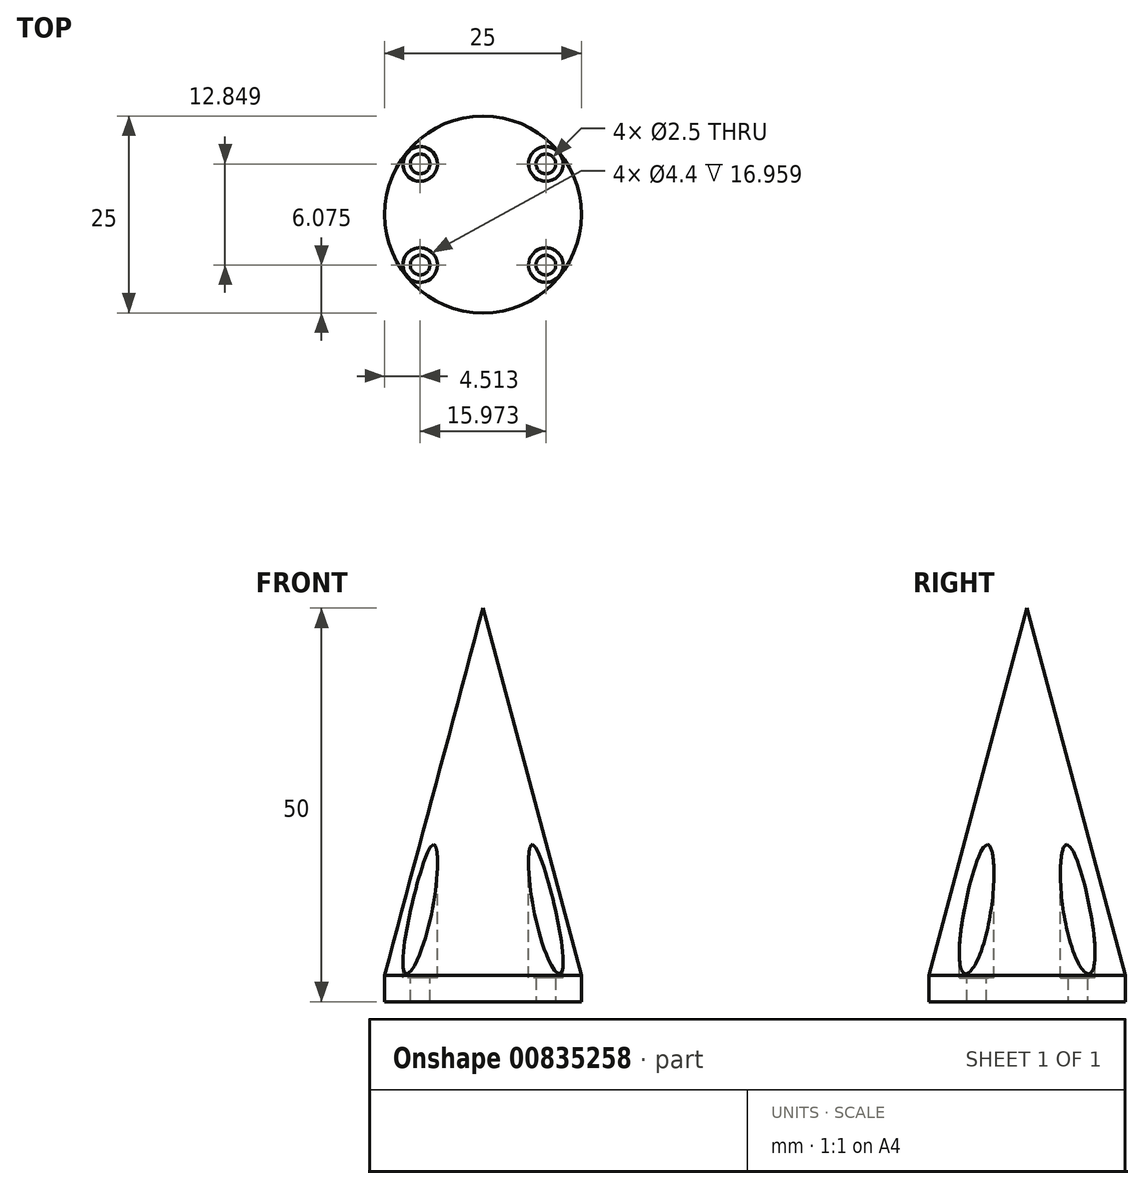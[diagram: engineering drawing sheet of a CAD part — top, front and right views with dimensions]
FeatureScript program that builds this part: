
annotation { "Feature Type Name" : "Feature", "Feature Type Description" : "" }
export const myFeature = defineFeature(function(context is Context, id is Id, definition is map)
    precondition{}
    {
        {
            var Q0;
            Q0=qCreatedBy(makeId("Top.planeOp"),FACE);
            var sketch = newSketch(context, id + "F0", { "sketchPlane" : qUnion([Q0])});
            skCircle(sketch, "E0", {"center": v(0, 0) * mm, "radius": 12.5 * mm});
            skPoint(sketch, "E1", {"position": v(-9.74, 7.83) * mm});
            skLineSegment(sketch, "E2", {"start": v(-9.74, 7.83) * mm, "end": v(9.74, -7.83) * mm, "construction": true});
            skPoint(sketch, "E3", {"position": v(-7.83, -9.74) * mm});
            skLineSegment(sketch, "E4", {"start": v(-7.83, -9.74) * mm, "end": v(7.83, 9.74) * mm, "construction": true});
            skPoint(sketch, "E5", {"position": v(0, 12.5) * mm});
            skPoint(sketch, "E6", {"position": v(-12.5, 0) * mm});
            skLineSegment(sketch, "E7", {"start": v(0, 12.5) * mm, "end": v(0, -12.5) * mm, "construction": true});
            skLineSegment(sketch, "E8", {"start": v(-12.5, 0) * mm, "end": v(12.5, 0) * mm, "construction": true});
            skPoint(sketch, "E9.third.point", {"position": v(-9.74, -7.83) * mm});
            skCircle(sketch, "E10", {"center": v(7.99, -6.42) * mm, "radius": 2.25 * mm});
            skPoint(sketch, "E10.second.point", {"position": v(6.23, -5.01) * mm});
            skPoint(sketch, "E10.third.point", {"position": v(6.23, -7.83) * mm});
            skCircle(sketch, "E11", {"center": v(7.99, -6.42) * mm, "radius": 1.25 * mm});
            skCircle(sketch, "E12.MirrorC", {"center": v(7.99, 6.42) * mm, "radius": 2.25 * mm});
            skCircle(sketch, "E13.MirrorC", {"center": v(7.99, 6.42) * mm, "radius": 1.25 * mm});
            skCircle(sketch, "E14.MirrorC", {"center": v(-7.99, -6.42) * mm, "radius": 1.25 * mm});
            skCircle(sketch, "E15.MirrorC", {"center": v(-7.99, -6.42) * mm, "radius": 2.25 * mm});
            skCircle(sketch, "E16.MirrorC", {"center": v(-7.99, 6.42) * mm, "radius": 2.25 * mm});
            skCircle(sketch, "E17.MirrorC", {"center": v(-7.99, 6.42) * mm, "radius": 1.25 * mm});
            skSolve(sketch);
        }
        {
            var Q0;
            Q0=makeQuery(id+"F0.imprint","IMPRINT",FACE,{"disambiguationData":[TD([[makeQuery(id+"F0.imprint","IMPRINT",EDGE,{"derivedFrom":sQuery(id+"F0.wireOp",EDGE,"E13.MirrorC")}),-1.0]])]});
            var Q1;
            Q1=makeQuery(id+"F0.imprint","IMPRINT",FACE,{"disambiguationData":[TD([[makeQuery(id+"F0.imprint","IMPRINT",EDGE,{"derivedFrom":sQuery(id+"F0.wireOp",EDGE,"E12.MirrorC")}),-1.0]])]});
            var Q2;
            {var subQ3=sQuery(id+"F0.wireOp",EDGE,"E10");Q2=makeQuery(id+"F0.imprint","IMPRINT",FACE,{"disambiguationData":[TD([[makeQuery(id+"F0.imprint","IMPRINT",EDGE,{"derivedFrom":subQ3}),-1.0]])]});}
            var Q3;
            Q3=makeQuery(id+"F0.imprint","IMPRINT",FACE,{"disambiguationData":[TD([[makeQuery(id+"F0.imprint","IMPRINT",EDGE,{"derivedFrom":sQuery(id+"F0.wireOp",EDGE,"E10")}),1.0]])]});
            var Q4;
            Q4=makeQuery(id+"F0.imprint","IMPRINT",FACE,{"disambiguationData":[TD([[makeQuery(id+"F0.imprint","IMPRINT",EDGE,{"derivedFrom":sQuery(id+"F0.wireOp",EDGE,"E11")}),1.0]])]});
            var Q5;
            Q5=makeQuery(id+"F0.imprint","IMPRINT",FACE,{"disambiguationData":[TD([[makeQuery(id+"F0.imprint","IMPRINT",EDGE,{"derivedFrom":sQuery(id+"F0.wireOp",EDGE,"E14.MirrorC")}),-1.0]])]});
            var Q6;
            Q6=makeQuery(id+"F0.imprint","IMPRINT",FACE,{"disambiguationData":[TD([[makeQuery(id+"F0.imprint","IMPRINT",EDGE,{"derivedFrom":sQuery(id+"F0.wireOp",EDGE,"E14.MirrorC")}),1.0]])]});
            var Q7;
            Q7=makeQuery(id+"F0.imprint","IMPRINT",FACE,{"disambiguationData":[TD([[makeQuery(id+"F0.imprint","IMPRINT",EDGE,{"derivedFrom":sQuery(id+"F0.wireOp",EDGE,"E16.MirrorC")}),1.0]])]});
            var Q8;
            Q8=makeQuery(id+"F0.imprint","IMPRINT",FACE,{"disambiguationData":[TD([[makeQuery(id+"F0.imprint","IMPRINT",EDGE,{"derivedFrom":sQuery(id+"F0.wireOp",EDGE,"E17.MirrorC")}),1.0]])]});
            extrude(context, id + "F1", {"entities" : qUnion([Q0, Q1, Q2, Q3, Q4, Q5, Q6, Q7, Q8]), "depth" : 5 * mm, "offsetDistance" : 25 * mm});
        }
        {
            var Q0;
            Q0=makeQuery(id+"F1.opExtrude","CAP_FACE",FACE,{"disambiguationData":[OSD([sQuery(id+"F0.wireOp",EDGE,"E0")])],"isStart":false});
            var sketch = newSketch(context, id + "F2", { "sketchPlane" : qUnion([Q0])});
            skPoint(sketch, "E18", {"position": v(-7.99, 6.42) * mm});
            skPoint(sketch, "E19", {"position": v(-7.99, -6.42) * mm});
            skPoint(sketch, "E20", {"position": v(7.99, -6.42) * mm});
            skPoint(sketch, "E21", {"position": v(7.99, 6.42) * mm});
            skSolve(sketch);
        }
        {
            var Q0;
            Q0=sQuery(id+"F2.wireOp",VERTEX,"E18");
            var Q1;
            Q1=sQuery(id+"F2.wireOp",VERTEX,"E19");
            var Q2;
            Q2=sQuery(id+"F2.wireOp",VERTEX,"E20");
            var Q3;
            Q3=sQuery(id+"F2.wireOp",VERTEX,"E21");
            var Q4;
            Q4=makeQuery(id+"F1.opExtrude","SWEPT_BODY",BODY,{"disambiguationData":[OSD([sQuery(id+"F0.wireOp",EDGE,"E0")])]});
            hole(context, id + "F3", {"style" : HoleStyle.C_BORE, "endStyle" : HoleEndStyle.BLIND, "holeDiameter" : 2.5 * mm, "cBoreDiameter" : 4.4 * mm, "cBoreDepth" : 2 * mm, "majorDiameter" : 5 * mm, "holeDepth" : 5 * mm, "isTappedThrough" : true, "tappedDepth" : 12 * mm, "tapClearance" : 3, "locations" : qUnion([Q0, Q1, Q2, Q3]), "scope" : qUnion([Q4])});
        }
        {
            var Q0;
            Q0=makeQuery(id+"F1.opExtrude","CAP_FACE",FACE,{"disambiguationData":[OSD([sQuery(id+"F0.wireOp",EDGE,"E0")])],"isStart":false});
            extrude(context, id + "F4", {"entities" : qUnion([Q0]), "operationType" : NewBodyOperationType.ADD, "depth" : 45 * mm, "offsetDistance" : 25 * mm});
        }
        {
            var Q0;
            Q0=makeQuery(id+"F4.opExtrude","CAP_EDGE",EDGE,{"disambiguationData":[OSD([sQuery(id+"F0.wireOp",EDGE,"E0")])],"isStart":false});
            chamfer(context, id + "F5", {"entities" : qUnion([Q0]), "chamferType" : ChamferType.OFFSET_ANGLE, "width" : 12.5 * mm, "oppositeDirection" : false, "angle" : 75 * degree, "tangentPropagation" : true});
        }
    });
